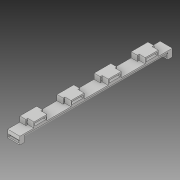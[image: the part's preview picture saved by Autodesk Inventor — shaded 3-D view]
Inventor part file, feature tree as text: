
AUTODESK INVENTOR PART (.ipt)
format: ipt  version: 2019 (Build 230136000, 136)  size: 576,000 bytes
history: native  units: mm
features: extrude x16, sketch x15, fillet x2
ambient origin geometry x8: Origin, YZ Plane, XZ Plane, XY Plane, X Axis, Y Axis, Z Axis, Center Point
bodies: Solid1 (feature_tree)
feature tree (33):
  extrude  "Extrusion1"  Depth=120.0mm
  extrude  "Extrusion2"  Depth=8.0mm
  extrude  "Extrusion3"  Depth=11.0mm
  extrude  "Extrusion4"  Depth=11.0mm
  extrude  "Extrusion5"  Depth=11.0mm
  extrude  "Extrusion6"  Depth=11.001mm
  extrude  "Extrusion7"  Depth=8.556mm
  extrude  "Extrusion8"  Depth=8.556mm
  extrude  "Extrusion9"  Depth=8.556mm
  extrude  "Extrusion10"  Depth=8.556mm
  extrude  "Extrusion11"  Depth=3.5mm TaperAngle=0.0deg
  extrude  "Extrusion12"  Depth=0.628mm
  extrude  "Extrusion13"  Depth=0.628mm
  extrude  "Extrusion14"  Depth=0.9mm
  extrude  "Extrusion15"  Depth=0.628mm
  extrude  "Extrusion16"  Depth=0.628mm
  fillet  "Fillet3"  Radius=4.0mm
  fillet  "Fillet4"  Radius=8.0mm
  sketch  "Sketch1"  dims[d0=8.0mm d1=120.0mm]
  sketch  "Sketch2"  dims[d2=2.5mm d3=0.0mm d4=8.0mm]
  sketch  "Sketch3"  dims[d5=28.0mm d6=11.0mm]
  sketch  "Sketch4"  dims[d7=13.333mm d8=11.0mm]
  sketch  "Sketch6"  dims[d9=13.333mm d10=11.0mm]
  sketch  "Sketch7"  dims[d11=13.333mm d12=11.001mm]
  sketch  "Sketch9"  dims[d13=9.222mm d14=8.556mm]
  sketch  "Sketch10"  dims[d15=15.777mm d16=8.556mm]
  sketch  "Sketch11"  dims[d17=15.777mm d18=8.556mm]
  sketch  "Sketch12"  dims[d19=15.777mm d20=8.556mm]
  sketch  "Sketch13"  dims[d21=29.223mm d22=3.5mm d23=0.0mm]
  sketch  "Sketch14"  dims[d25=0.9mm d26=0.628mm]
  sketch  "Sketch15"  dims[d27=0.9mm d28=0.628mm]
  sketch  "Sketch16"  dims[d29=4.0mm d30=0.0mm d31=0.9mm]
  sketch  "Sketch17"  dims[d32=0.9mm d33=0.628mm d34=0.628mm d35=4.0mm d36=0.0mm d37=8.0mm d38=3.0mm d39=8.0mm d40=3.0mm d41=2.5mm d42=0.0mm d43=0.9mm d44=0.628mm d45=6.744mm d46=1.362mm d47=3.0mm d48=0.0mm d49=0.9mm d50=0.628mm d51=3.0mm d52=0.0mm d53=0.9mm d54=0.628mm d55=0.9mm d56=0.628mm d57=4.0mm d58=0.0mm d59=0.9mm d60=0.628mm d62=0.628mm d63=4.0mm d64=0.0mm d65=0.9mm d66=0.628mm d67=0.9mm d68=0.628mm d69=7.3mm d70=4.0mm d71=0.0mm d72=0.9mm d73=0.628mm d74=0.9mm d75=0.628mm d76=0.628mm d77=4.0mm d78=0.0mm d79=0.9mm d80=0.628mm d81=0.9mm d82=0.628mm d83=4.0mm d84=0.0mm d86=0.628mm d88=0.628mm d89=4.0mm d90=0.0mm d93=1.223mm d94=8.0mm d95=10.0mm d96=0.0mm d97=8.0mm d98=3.0mm d99=2.5mm d100=0.0mm d101=0.9mm d102=0.628mm d103=3.0mm d104=0.0mm d105=1.5mm d106=1.5mm]
